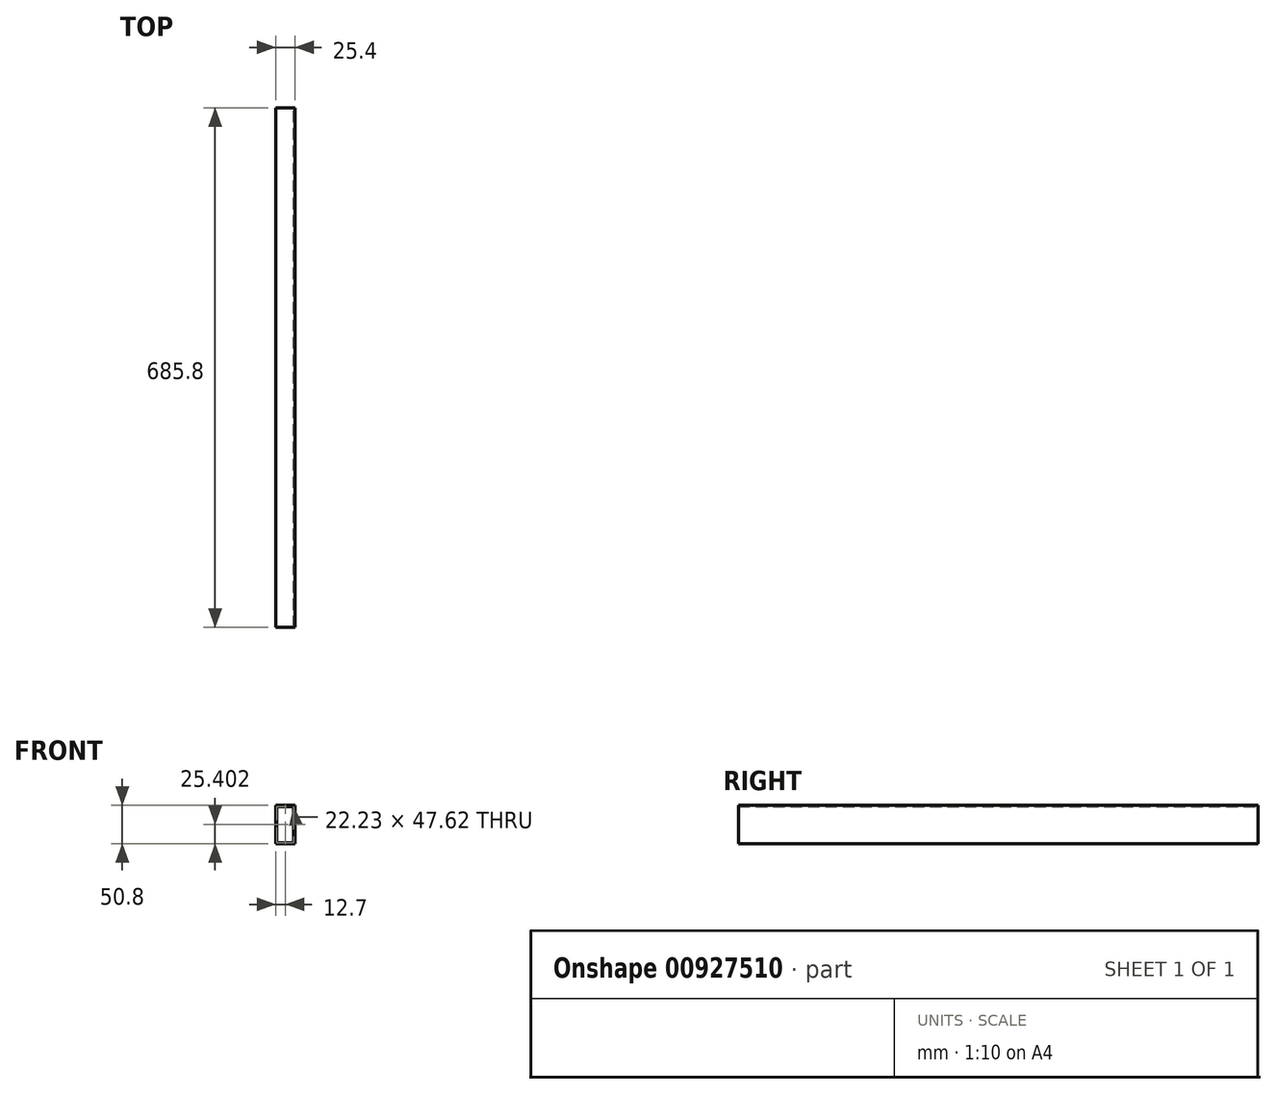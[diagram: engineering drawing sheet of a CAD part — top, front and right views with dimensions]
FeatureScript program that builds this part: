
annotation { "Feature Type Name" : "Feature", "Feature Type Description" : "" }
export const myFeature = defineFeature(function(context is Context, id is Id, definition is map)
    precondition{}
    {
        {
            var Q0;
            Q0=qCreatedBy(makeId("Front.planeOp"),FACE);
            var sketch = newSketch(context, id + "F0", { "sketchPlane" : qUnion([Q0])});
            skLineSegment(sketch, "E0.bottom", {"start": v(7.99, 32.2) * mm, "end": v(33.39, 32.2) * mm});
            skLineSegment(sketch, "E0.top", {"start": v(7.99, -18.6) * mm, "end": v(33.39, -18.6) * mm});
            skLineSegment(sketch, "E0.left", {"start": v(7.99, 32.2) * mm, "end": v(7.99, -18.6) * mm});
            skLineSegment(sketch, "E0.right", {"start": v(33.39, 32.2) * mm, "end": v(33.39, -18.6) * mm});
            skLineSegment(sketch, "E1.bottom", {"start": v(9.58, 30.6) * mm, "end": v(31.8, 30.6) * mm});
            skLineSegment(sketch, "E1.top", {"start": v(9.58, -17.02) * mm, "end": v(31.8, -17.02) * mm});
            skLineSegment(sketch, "E1.left", {"start": v(9.58, 30.6) * mm, "end": v(9.58, -17.02) * mm});
            skLineSegment(sketch, "E1.right", {"start": v(31.8, 30.6) * mm, "end": v(31.8, -17.02) * mm});
            skSolve(sketch);
        }
        {
            var Q0;
            Q0=makeQuery(id+"F0.imprint","IMPRINT",FACE,{"disambiguationData":[TD([[makeQuery(id+"F0.imprint","IMPRINT",EDGE,{"derivedFrom":sQuery(id+"F0.wireOp",EDGE,"E0.bottom")}),-1.0]])]});
            extrude(context, id + "F1", {"entities" : qUnion([Q0]), "depth" : 685.8 * mm, "offsetDistance" : 25.4 * mm});
        }
    });
